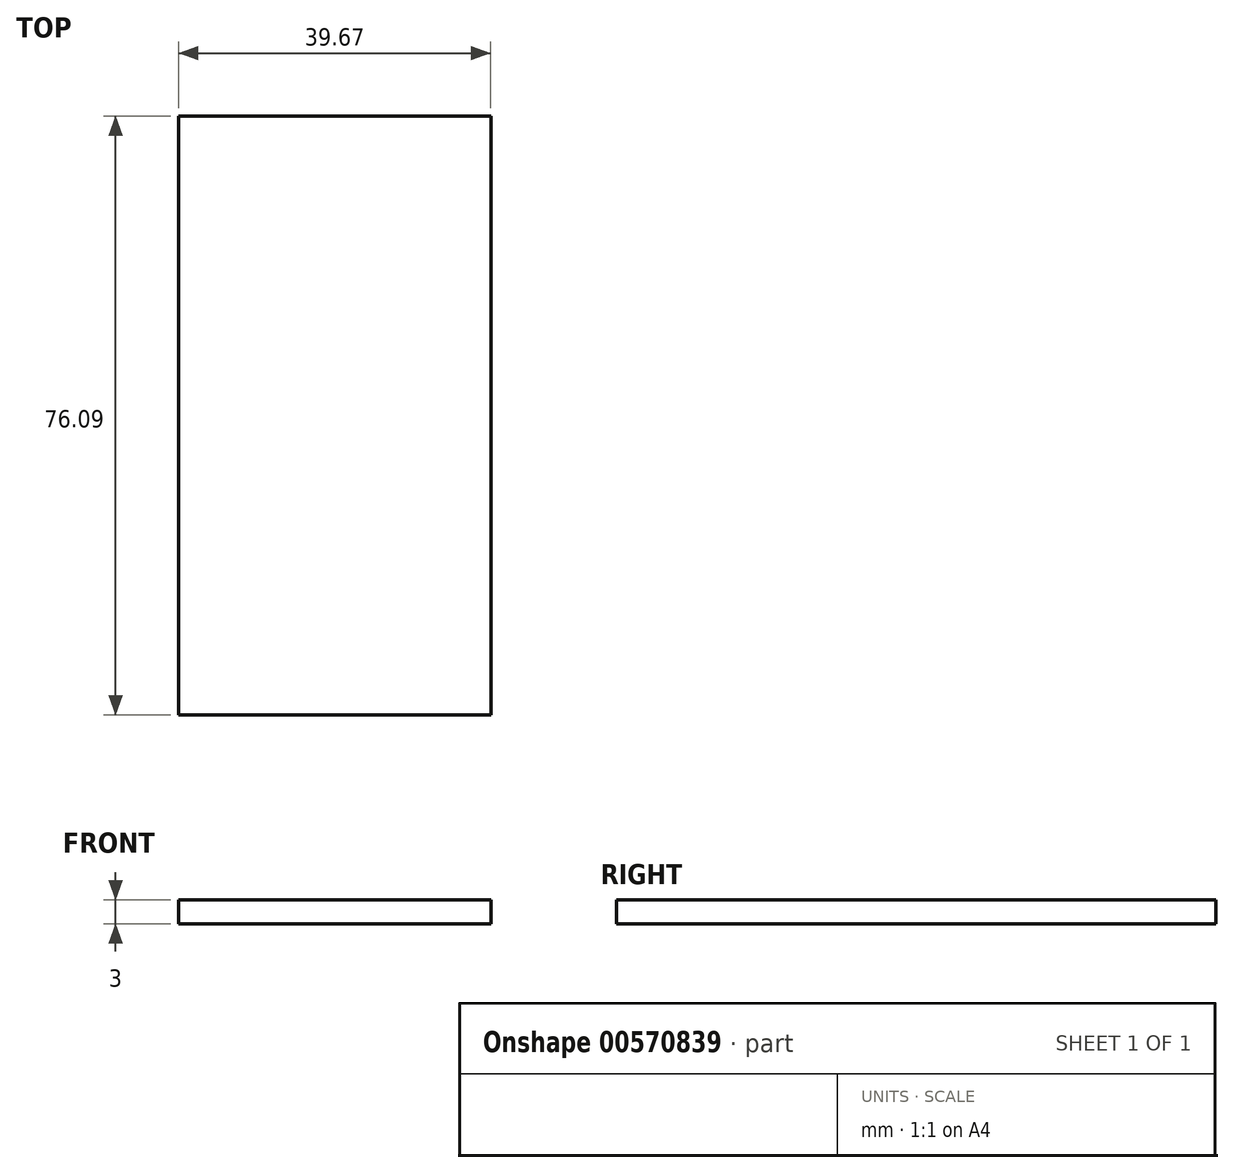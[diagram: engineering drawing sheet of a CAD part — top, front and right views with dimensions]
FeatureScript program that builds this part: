
annotation { "Feature Type Name" : "Feature", "Feature Type Description" : "" }
export const myFeature = defineFeature(function(context is Context, id is Id, definition is map)
    precondition{}
    {
        {
            var Q0;
            Q0=qCreatedBy(makeId("Top.planeOp"),FACE);
            var sketch = newSketch(context, id + "F0", { "sketchPlane" : qUnion([Q0])});
            skSolve(sketch);
        }
        {
            var Q0;
            Q0=qCreatedBy(makeId("Top.planeOp"),FACE);
            var sketch = newSketch(context, id + "F1", { "sketchPlane" : qUnion([Q0])});
            skLineSegment(sketch, "E0.bottom", {"start": v(0, 0) * mm, "end": v(39.67, 0) * mm});
            skLineSegment(sketch, "E0.top", {"start": v(0, 76.09) * mm, "end": v(39.67, 76.09) * mm});
            skLineSegment(sketch, "E0.left", {"start": v(0, 0) * mm, "end": v(0, 76.09) * mm});
            skLineSegment(sketch, "E0.right", {"start": v(39.67, 0) * mm, "end": v(39.67, 76.09) * mm});
            skSolve(sketch);
        }
        {
            var Q0;
            Q0=makeQuery(id+"F1.imprint","IMPRINT",FACE,{"disambiguationData":[TD([[makeQuery(id+"F1.imprint","IMPRINT",EDGE,{"derivedFrom":sQuery(id+"F1.wireOp",EDGE,"E0.bottom")}),1.0]])]});
            extrude(context, id + "F2", {"entities" : qUnion([Q0]), "depth" : 3 * mm, "offsetDistance" : 25 * mm});
        }
    });
